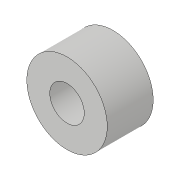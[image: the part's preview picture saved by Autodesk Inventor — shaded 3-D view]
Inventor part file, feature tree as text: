
AUTODESK INVENTOR PART (.ipt)
format: ipt  version: 2018.3 (Build 223284000, 284)  size: 81,920 bytes
history: native  units: in
note: dims shown in document units (in); Inventor stores cm internally (conversion verified against a paired STEP export)
features: extrude x1, sketch x1
ambient origin geometry x8: Origin, YZ Plane, XZ Plane, XY Plane, X Axis, Y Axis, Z Axis, Center Point
bodies: Solid1 (feature_tree)
feature tree (2):
  extrude  "Extrusion1"  Depth=0.5in
  sketch  "Sketch1"  dims[d0=0.375in d1=0.875in d2=0.5in d3=0.0in]
